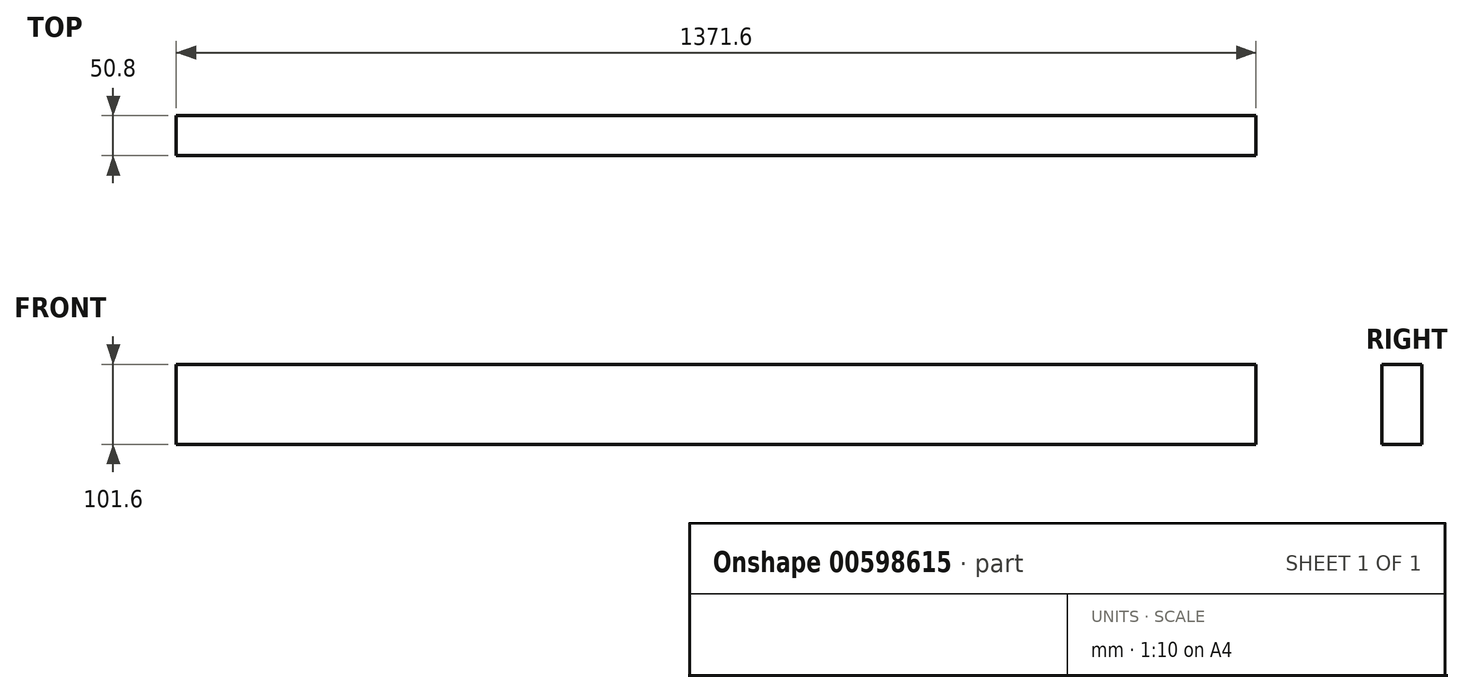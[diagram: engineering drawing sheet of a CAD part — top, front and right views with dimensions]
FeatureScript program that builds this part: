
annotation { "Feature Type Name" : "Feature", "Feature Type Description" : "" }
export const myFeature = defineFeature(function(context is Context, id is Id, definition is map)
    precondition{}
    {
        {
            var Q0;
            Q0=qCreatedBy(makeId("Top.planeOp"),FACE);
            var sketch = newSketch(context, id + "F0", { "sketchPlane" : qUnion([Q0])});
            skLineSegment(sketch, "E0.bottom", {"start": v(-692.41, -177.55) * mm, "end": v(679.19, -177.55) * mm});
            skLineSegment(sketch, "E0.top", {"start": v(-692.41, -228.35) * mm, "end": v(679.19, -228.35) * mm});
            skLineSegment(sketch, "E0.left", {"start": v(-692.41, -177.55) * mm, "end": v(-692.41, -228.35) * mm});
            skLineSegment(sketch, "E0.right", {"start": v(679.19, -177.55) * mm, "end": v(679.19, -228.35) * mm});
            skSolve(sketch);
        }
        {
            var Q0;
            Q0=makeQuery(id+"F0.imprint","IMPRINT",FACE,{"disambiguationData":[TD([[makeQuery(id+"F0.imprint","IMPRINT",EDGE,{"derivedFrom":sQuery(id+"F0.wireOp",EDGE,"E0.bottom")}),-1.0]])]});
            extrude(context, id + "F1", {"entities" : qUnion([Q0]), "depth" : 101.6 * mm, "offsetDistance" : 25.4 * mm});
        }
    });
